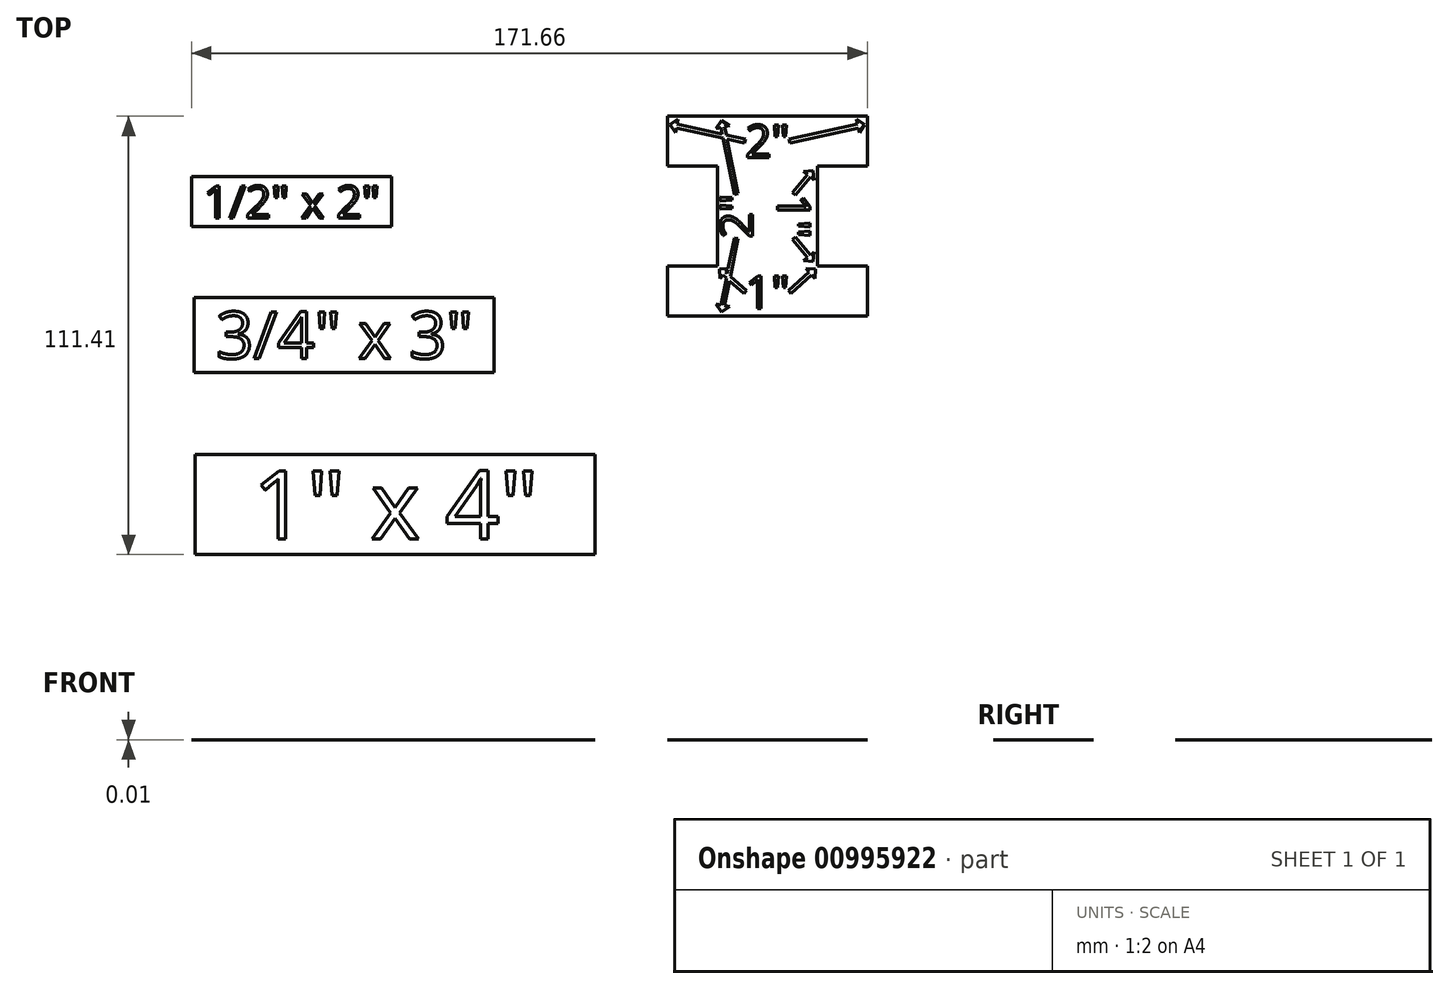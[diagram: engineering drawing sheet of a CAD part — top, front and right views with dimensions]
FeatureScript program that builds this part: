
annotation { "Feature Type Name" : "Feature", "Feature Type Description" : "" }
export const myFeature = defineFeature(function(context is Context, id is Id, definition is map)
    precondition{}
    {
        {
            var Q0;
            Q0=qCreatedBy(makeId("Top.planeOp"),FACE);
            var sketch = newSketch(context, id + "F0", { "sketchPlane" : qUnion([Q0])});
            skLineSegment(sketch, "E0.bottom", {"start": v(-26.28, -9.14) * mm, "end": v(24.52, -9.14) * mm});
            skLineSegment(sketch, "E0.top", {"start": v(-26.28, -21.84) * mm, "end": v(24.52, -21.84) * mm});
            skLineSegment(sketch, "E0.left", {"start": v(-26.28, -9.14) * mm, "end": v(-26.28, -21.84) * mm});
            skLineSegment(sketch, "E0.right", {"start": v(24.52, -9.14) * mm, "end": v(24.52, -21.84) * mm});
            skLineSegment(sketch, "E1.bottom", {"start": v(-25.6, -39.82) * mm, "end": v(50.6, -39.82) * mm});
            skLineSegment(sketch, "E1.top", {"start": v(-25.6, -58.87) * mm, "end": v(50.6, -58.87) * mm});
            skLineSegment(sketch, "E1.left", {"start": v(-25.6, -39.82) * mm, "end": v(-25.6, -58.87) * mm});
            skLineSegment(sketch, "E1.right", {"start": v(50.6, -39.82) * mm, "end": v(50.6, -58.87) * mm});
            skLineSegment(sketch, "E2.bottom", {"start": v(-25.36, -79.76) * mm, "end": v(76.24, -79.76) * mm});
            skLineSegment(sketch, "E2.top", {"start": v(-25.36, -105.16) * mm, "end": v(76.24, -105.16) * mm});
            skLineSegment(sketch, "E2.left", {"start": v(-25.36, -79.76) * mm, "end": v(-25.36, -105.16) * mm});
            skLineSegment(sketch, "E2.right", {"start": v(76.24, -79.76) * mm, "end": v(76.24, -105.16) * mm});
            skLineSegment(sketch, "E3", {"start": v(94.58, 6.25) * mm, "end": v(145.38, 6.25) * mm});
            skLineSegment(sketch, "E4", {"start": v(145.38, 6.25) * mm, "end": v(145.38, -6.45) * mm});
            skLineSegment(sketch, "E5", {"start": v(145.38, -6.45) * mm, "end": v(132.68, -6.45) * mm});
            skLineSegment(sketch, "E6", {"start": v(132.68, -6.45) * mm, "end": v(132.68, -31.85) * mm});
            skLineSegment(sketch, "E7", {"start": v(132.68, -31.85) * mm, "end": v(145.38, -31.85) * mm});
            skLineSegment(sketch, "E8", {"start": v(145.38, -31.85) * mm, "end": v(145.38, -44.55) * mm});
            skLineSegment(sketch, "E9", {"start": v(145.38, -44.55) * mm, "end": v(94.58, -44.55) * mm});
            skLineSegment(sketch, "E10", {"start": v(94.58, -44.55) * mm, "end": v(94.58, -31.85) * mm});
            skLineSegment(sketch, "E11", {"start": v(94.58, -31.85) * mm, "end": v(107.28, -31.85) * mm});
            skLineSegment(sketch, "E12", {"start": v(107.28, -31.85) * mm, "end": v(107.28, -6.45) * mm});
            skLineSegment(sketch, "E13", {"start": v(107.28, -6.45) * mm, "end": v(94.58, -6.45) * mm});
            skLineSegment(sketch, "E14", {"start": v(94.58, -6.45) * mm, "end": v(94.58, 6.25) * mm});
            skLineSegment(sketch, "E15", {"start": v(107.28, -6.45) * mm, "end": v(132.68, -6.45) * mm, "construction": true});
            skSolve(sketch);
        }
        {
            var Q0;
            Q0 = qSketchRegion(id + "F0", true);
            extrude(context, id + "F1", {"entities" : qUnion([Q0]), "depth" : 1 / 101.6 * mm, "offsetDistance" : 25 * mm});
        }
        {
            var Q0;
            Q0=makeQuery(id+"F1.opExtrude","CAP_FACE",FACE,{"disambiguationData":[OSD([sQuery(id+"F0.wireOp",EDGE,"E0.bottom"),sQuery(id+"F0.wireOp",EDGE,"E0.top"),sQuery(id+"F0.wireOp",EDGE,"E0.left"),sQuery(id+"F0.wireOp",EDGE,"E0.right")])],"isStart":false});
            var sketch = newSketch(context, id + "F2", { "sketchPlane" : qUnion([Q0])});
            skText(sketch, "E16", { "text": "1/2\" x 2\"", "fontName": "OpenSans-Regular.ttf"});
            skPoint(sketch, "E17", {"position": v(-23.3, -15.5) * mm});
            skPoint(sketch, "E18.positionSnap0", {"position": v(-0.88, -21.84) * mm});
            skPoint(sketch, "E19", {"position": v(-26.28, -15.5) * mm});
            const initialGuessF2  = {"E16": [-0.0233, -0.0196, 1, 0, 0.00822]};
            skSetInitialGuess(sketch, initialGuessF2);
            skSolve(sketch);
        }
        {
            var Q0;
            Q0=makeQuery(id+"F1.opExtrude","CAP_FACE",FACE,{"disambiguationData":[OSD([sQuery(id+"F0.wireOp",EDGE,"E1.bottom"),sQuery(id+"F0.wireOp",EDGE,"E1.top"),sQuery(id+"F0.wireOp",EDGE,"E1.left"),sQuery(id+"F0.wireOp",EDGE,"E1.right")])],"isStart":false});
            var sketch = newSketch(context, id + "F3", { "sketchPlane" : qUnion([Q0])});
            skText(sketch, "E20", { "text": "3/4\" x 3\"", "fontName": "OpenSans-Regular.ttf"});
            skPoint(sketch, "E21", {"position": v(-20.1, -49.34) * mm});
            skPoint(sketch, "E22.positionSnap0", {"position": v(12.5, -58.87) * mm});
            skPoint(sketch, "E23", {"position": v(-25.6, -49.34) * mm});
            const initialGuessF3  = {"E20": [-0.0201, -0.05531, 1, 0, 0.01195]};
            skSetInitialGuess(sketch, initialGuessF3);
            skSolve(sketch);
        }
        {
            var Q0;
            Q0=makeQuery(id+"F1.opExtrude","CAP_FACE",FACE,{"disambiguationData":[OSD([sQuery(id+"F0.wireOp",EDGE,"E2.bottom"),sQuery(id+"F0.wireOp",EDGE,"E2.top"),sQuery(id+"F0.wireOp",EDGE,"E2.left"),sQuery(id+"F0.wireOp",EDGE,"E2.right")])],"isStart":false});
            var sketch = newSketch(context, id + "F4", { "sketchPlane" : qUnion([Q0])});
            skText(sketch, "E24", { "text": "1\" x 4\"", "fontName": "OpenSans-Regular.ttf"});
            skPoint(sketch, "E25", {"position": v(-10.93, -92.46) * mm});
            skPoint(sketch, "E26.positionSnap0", {"position": v(25.44, -105.16) * mm});
            skPoint(sketch, "E27", {"position": v(-25.36, -92.46) * mm});
            const initialGuessF4  = {"E24": [-0.01093, -0.10122, 1, 0, 0.01752]};
            skSetInitialGuess(sketch, initialGuessF4);
            skSolve(sketch);
        }
        {
            var Q0;
            Q0=makeQuery(id+"F1.opExtrude","CAP_FACE",FACE,{"disambiguationData":[OSD([sQuery(id+"F0.wireOp",EDGE,"E3"),sQuery(id+"F0.wireOp",EDGE,"E4"),sQuery(id+"F0.wireOp",EDGE,"E5"),sQuery(id+"F0.wireOp",EDGE,"E6"),sQuery(id+"F0.wireOp",EDGE,"E7"),sQuery(id+"F0.wireOp",EDGE,"E8"),sQuery(id+"F0.wireOp",EDGE,"E9"),sQuery(id+"F0.wireOp",EDGE,"E10"),sQuery(id+"F0.wireOp",EDGE,"E11"),sQuery(id+"F0.wireOp",EDGE,"E12"),sQuery(id+"F0.wireOp",EDGE,"E13"),sQuery(id+"F0.wireOp",EDGE,"E14")])],"isStart":false});
            var sketch = newSketch(context, id + "F5", { "sketchPlane" : qUnion([Q0])});
            skText(sketch, "E28", { "text": "2\"", "fontName": "OpenSans-Regular.ttf"});
            skPoint(sketch, "E29", {"position": v(114.34, -0.1) * mm});
            skPoint(sketch, "E30.positionSnap0", {"position": v(119.98, 6.25) * mm});
            skPoint(sketch, "E31", {"position": v(94.58, -0.1) * mm});
            skLineSegment(sketch, "E32", {"start": v(114.34, -0.1) * mm, "end": v(96.97, 3.78) * mm, "construction": true});
            skLineSegment(sketch, "E33.0", {"start": v(114.45, 0.4) * mm, "end": v(97.08, 4.26) * mm});
            skLineSegment(sketch, "E34.0", {"start": v(114.23, -0.58) * mm, "end": v(96.86, 3.29) * mm});
            skLineSegment(sketch, "E35", {"start": v(96.86, 3.29) * mm, "end": v(97.08, 4.26) * mm, "construction": true});
            skLineSegment(sketch, "E36", {"start": v(114.23, -0.58) * mm, "end": v(114.45, 0.4) * mm});
            skLineSegment(sketch, "E37", {"start": v(96.86, 3.29) * mm, "end": v(96.6, 2.1) * mm});
            skLineSegment(sketch, "E38", {"start": v(96.6, 2.1) * mm, "end": v(95.29, 4.15) * mm});
            skLineSegment(sketch, "E39", {"start": v(95.29, 4.15) * mm, "end": v(97.34, 5.46) * mm});
            skLineSegment(sketch, "E40", {"start": v(97.34, 5.46) * mm, "end": v(97.08, 4.26) * mm});
            skLineSegment(sketch, "E41.MirrorCS", {"start": v(125.63, -0.1) * mm, "end": v(143, 3.78) * mm, "construction": true});
            skLineSegment(sketch, "E42.MirrorCS", {"start": v(143.1, 3.29) * mm, "end": v(142.89, 4.26) * mm, "construction": true});
            skLineSegment(sketch, "E43.MirrorCS", {"start": v(125.74, -0.58) * mm, "end": v(125.52, 0.4) * mm});
            skLineSegment(sketch, "E44.MirrorCS", {"start": v(142.62, 5.46) * mm, "end": v(142.89, 4.26) * mm});
            skLineSegment(sketch, "E45.MirrorCS", {"start": v(143.1, 3.29) * mm, "end": v(143.37, 2.1) * mm});
            skPoint(sketch, "E46.MirrorP", {"position": v(125.63, -0.1) * mm});
            skLineSegment(sketch, "E47.MirrorCS", {"start": v(143.37, 2.1) * mm, "end": v(144.68, 4.15) * mm});
            skLineSegment(sketch, "E48.MirrorCS", {"start": v(144.68, 4.15) * mm, "end": v(142.62, 5.46) * mm});
            skPoint(sketch, "E49.MirrorP", {"position": v(145.38, -0.1) * mm});
            skLineSegment(sketch, "E50.MirrorCS", {"start": v(125.74, -0.58) * mm, "end": v(143.1, 3.29) * mm});
            skLineSegment(sketch, "E51.MirrorCS", {"start": v(125.52, 0.4) * mm, "end": v(142.89, 4.26) * mm});
            skText(sketch, "E52", { "text": "2\"", "fontName": "OpenSans-Regular.ttf"});
            skPoint(sketch, "E53", {"position": v(112.09, -24.79) * mm});
            skPoint(sketch, "E54.positionSnap0", {"position": v(107.28, -19.15) * mm});
            skPoint(sketch, "E55", {"position": v(112.09, -44.55) * mm});
            skLineSegment(sketch, "E56", {"start": v(112.09, -24.79) * mm, "end": v(108.65, -41.8) * mm, "construction": true});
            skLineSegment(sketch, "E57.0", {"start": v(111.6, -24.7) * mm, "end": v(108.16, -41.7) * mm});
            skLineSegment(sketch, "E58.0", {"start": v(112.58, -24.89) * mm, "end": v(109.14, -41.9) * mm});
            skLineSegment(sketch, "E59", {"start": v(109.14, -41.9) * mm, "end": v(108.16, -41.7) * mm, "construction": true});
            skLineSegment(sketch, "E60", {"start": v(112.58, -24.89) * mm, "end": v(111.6, -24.7) * mm});
            skLineSegment(sketch, "E61", {"start": v(109.14, -41.9) * mm, "end": v(110.34, -42.14) * mm});
            skLineSegment(sketch, "E62", {"start": v(110.34, -42.14) * mm, "end": v(108.3, -43.49) * mm});
            skLineSegment(sketch, "E63", {"start": v(108.3, -43.49) * mm, "end": v(106.96, -41.46) * mm});
            skLineSegment(sketch, "E64", {"start": v(106.96, -41.46) * mm, "end": v(108.16, -41.7) * mm});
            skLineSegment(sketch, "E65.MirrorCS", {"start": v(112.09, -13.5) * mm, "end": v(108.65, 3.5) * mm, "construction": true});
            skLineSegment(sketch, "E66.MirrorCS", {"start": v(109.14, 3.6) * mm, "end": v(108.16, 3.4) * mm, "construction": true});
            skLineSegment(sketch, "E67.MirrorCS", {"start": v(112.58, -13.4) * mm, "end": v(111.6, -13.6) * mm});
            skLineSegment(sketch, "E68.MirrorCS", {"start": v(106.96, 3.16) * mm, "end": v(108.16, 3.4) * mm});
            skLineSegment(sketch, "E69.MirrorCS", {"start": v(109.14, 3.6) * mm, "end": v(110.34, 3.84) * mm});
            skPoint(sketch, "E70.MirrorP", {"position": v(112.09, -13.5) * mm});
            skLineSegment(sketch, "E71.MirrorCS", {"start": v(110.34, 3.84) * mm, "end": v(108.3, 5.2) * mm});
            skLineSegment(sketch, "E72.MirrorCS", {"start": v(108.3, 5.2) * mm, "end": v(106.96, 3.16) * mm});
            skPoint(sketch, "E73.MirrorP", {"position": v(112.09, 6.25) * mm});
            skLineSegment(sketch, "E74.MirrorCS", {"start": v(112.58, -13.4) * mm, "end": v(109.14, 3.6) * mm});
            skLineSegment(sketch, "E75.MirrorCS", {"start": v(111.6, -13.6) * mm, "end": v(108.16, 3.4) * mm});
            skText(sketch, "E76", { "text": "1\"", "fontName": "OpenSans-Regular.ttf"});
            skPoint(sketch, "E77", {"position": v(126.73, -13.5) * mm});
            skPoint(sketch, "E78.positionSnap0", {"position": v(132.68, -19.15) * mm});
            skPoint(sketch, "E79", {"position": v(126.73, 6.25) * mm});
            skLineSegment(sketch, "E80", {"start": v(126.73, -13.5) * mm, "end": v(130.51, -8.9) * mm, "construction": true});
            skLineSegment(sketch, "E81.0", {"start": v(127.11, -13.82) * mm, "end": v(130.9, -9.22) * mm});
            skLineSegment(sketch, "E82.0", {"start": v(126.34, -13.19) * mm, "end": v(130.13, -8.58) * mm});
            skLineSegment(sketch, "E83", {"start": v(130.13, -8.58) * mm, "end": v(130.9, -9.22) * mm, "construction": true});
            skLineSegment(sketch, "E84", {"start": v(126.34, -13.19) * mm, "end": v(127.11, -13.82) * mm});
            skLineSegment(sketch, "E85", {"start": v(130.13, -8.58) * mm, "end": v(129.18, -7.8) * mm});
            skLineSegment(sketch, "E86", {"start": v(129.18, -7.8) * mm, "end": v(131.6, -7.57) * mm});
            skLineSegment(sketch, "E87", {"start": v(131.6, -7.57) * mm, "end": v(131.84, -10) * mm});
            skLineSegment(sketch, "E88", {"start": v(131.84, -10) * mm, "end": v(130.9, -9.22) * mm});
            skLineSegment(sketch, "E89.MirrorCS", {"start": v(126.73, -24.79) * mm, "end": v(130.51, -29.4) * mm, "construction": true});
            skLineSegment(sketch, "E90.MirrorCS", {"start": v(130.13, -29.71) * mm, "end": v(130.9, -29.08) * mm, "construction": true});
            skLineSegment(sketch, "E91.MirrorCS", {"start": v(126.34, -25.1) * mm, "end": v(127.11, -24.47) * mm});
            skLineSegment(sketch, "E92.MirrorCS", {"start": v(131.84, -28.3) * mm, "end": v(130.9, -29.08) * mm});
            skLineSegment(sketch, "E93.MirrorCS", {"start": v(130.13, -29.71) * mm, "end": v(129.18, -30.49) * mm});
            skPoint(sketch, "E94.MirrorP", {"position": v(126.73, -24.79) * mm});
            skLineSegment(sketch, "E95.MirrorCS", {"start": v(129.18, -30.49) * mm, "end": v(131.6, -30.72) * mm});
            skLineSegment(sketch, "E96.MirrorCS", {"start": v(131.6, -30.72) * mm, "end": v(131.84, -28.3) * mm});
            skPoint(sketch, "E97.MirrorP", {"position": v(126.73, -44.55) * mm});
            skLineSegment(sketch, "E98.MirrorCS", {"start": v(126.34, -25.1) * mm, "end": v(130.13, -29.71) * mm});
            skLineSegment(sketch, "E99.MirrorCS", {"start": v(127.11, -24.47) * mm, "end": v(130.9, -29.08) * mm});
            skText(sketch, "E100", { "text": "1\"", "fontName": "OpenSans-Regular.ttf"});
            skPoint(sketch, "E101", {"position": v(114.34, -38.43) * mm});
            skPoint(sketch, "E102.positionSnap0", {"position": v(119.98, -44.55) * mm});
            skLineSegment(sketch, "E103", {"start": v(114.34, -38.43) * mm, "end": v(109.06, -33.73) * mm, "construction": true});
            skLineSegment(sketch, "E104.0", {"start": v(114.67, -38.06) * mm, "end": v(109.39, -33.35) * mm});
            skLineSegment(sketch, "E105.0", {"start": v(114, -38.8) * mm, "end": v(108.72, -34.1) * mm});
            skLineSegment(sketch, "E106", {"start": v(108.72, -34.1) * mm, "end": v(109.39, -33.35) * mm, "construction": true});
            skLineSegment(sketch, "E107", {"start": v(114, -38.8) * mm, "end": v(114.67, -38.06) * mm});
            skLineSegment(sketch, "E108", {"start": v(108.72, -34.1) * mm, "end": v(107.91, -35.01) * mm});
            skLineSegment(sketch, "E109", {"start": v(107.91, -35.01) * mm, "end": v(107.77, -32.58) * mm});
            skLineSegment(sketch, "E110", {"start": v(107.77, -32.58) * mm, "end": v(110.2, -32.44) * mm});
            skLineSegment(sketch, "E111", {"start": v(110.2, -32.44) * mm, "end": v(109.39, -33.35) * mm});
            skLineSegment(sketch, "E112.MirrorCS", {"start": v(125.63, -38.43) * mm, "end": v(130.91, -33.73) * mm, "construction": true});
            skLineSegment(sketch, "E113.MirrorCS", {"start": v(131.24, -34.1) * mm, "end": v(130.58, -33.35) * mm, "construction": true});
            skLineSegment(sketch, "E114.MirrorCS", {"start": v(125.96, -38.8) * mm, "end": v(125.3, -38.06) * mm});
            skLineSegment(sketch, "E115.MirrorCS", {"start": v(129.77, -32.44) * mm, "end": v(130.58, -33.35) * mm});
            skLineSegment(sketch, "E116.MirrorCS", {"start": v(131.24, -34.1) * mm, "end": v(132.06, -35.01) * mm});
            skPoint(sketch, "E117.MirrorP", {"position": v(125.63, -38.43) * mm});
            skLineSegment(sketch, "E118.MirrorCS", {"start": v(132.06, -35.01) * mm, "end": v(132.2, -32.58) * mm});
            skLineSegment(sketch, "E119.MirrorCS", {"start": v(132.2, -32.58) * mm, "end": v(129.77, -32.44) * mm});
            skLineSegment(sketch, "E120.MirrorCS", {"start": v(125.96, -38.8) * mm, "end": v(131.24, -34.1) * mm});
            skLineSegment(sketch, "E121.MirrorCS", {"start": v(125.3, -38.06) * mm, "end": v(130.58, -33.35) * mm});
            const initialGuessF5  = {"E28": [0.11434, -0.00427, 1, 0, 0.00836], "E52": [0.11626, -0.02479, 0, 1, 0.00836], "E76": [0.12255, -0.0135, 0, -1, 0.00836], "E100": [0.11434, -0.0426, 1, 0, 0.00836]};
            skSetInitialGuess(sketch, initialGuessF5);
            skSolve(sketch);
        }
        {
            var Q0;
            Q0 = qSketchRegion(id + "F2", true);
            var Q1;
            Q1 = qSketchRegion(id + "F3", true);
            var Q2;
            Q2 = qSketchRegion(id + "F4", true);
            var Q3;
            Q3 = qSketchRegion(id + "F5", true);
            extrude(context, id + "F6", {"entities" : qUnion([Q0, Q1, Q2, Q3]), "operationType" : NewBodyOperationType.REMOVE, "oppositeDirection" : true, "depth" : 1 / 203.2 * mm, "offsetDistance" : 25 * mm, "hasDraft" : true, "draftAngle" : 10 * degree, "draftPullDirection" : true});
        }
    });
